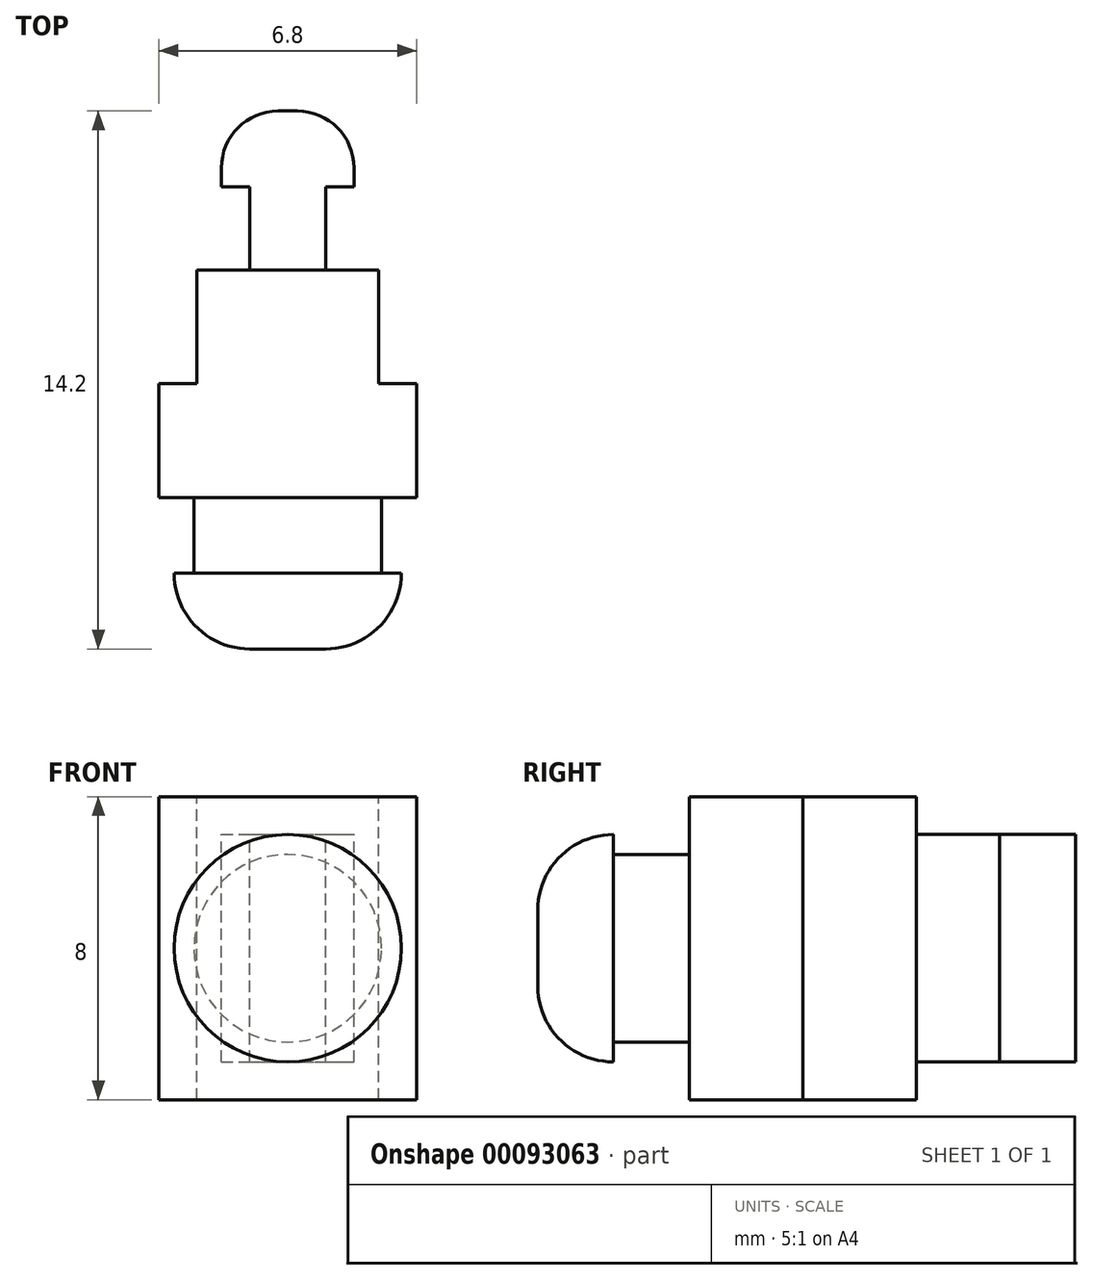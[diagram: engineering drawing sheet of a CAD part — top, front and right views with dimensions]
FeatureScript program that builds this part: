
annotation { "Feature Type Name" : "Feature", "Feature Type Description" : "" }
export const myFeature = defineFeature(function(context is Context, id is Id, definition is map)
    precondition{}
    {
        {
            var Q0;
            Q0=qCreatedBy(makeId("Front.planeOp"),FACE);
            var sketch = newSketch(context, id + "F0", { "sketchPlane" : qUnion([Q0])});
            skCircle(sketch, "E0", {"center": v(0, 0) * mm, "radius": 2.48 * mm});
            skSolve(sketch);
        }
        {
            var Q0;
            Q0=makeQuery(id+"F0.imprint","IMPRINT",FACE,{"disambiguationData":[TD([[makeQuery(id+"F0.imprint","IMPRINT",EDGE,{"derivedFrom":sQuery(id+"F0.wireOp",EDGE,"E0")}),1.0]])]});
            extrude(context, id + "F1", {"entities" : qUnion([Q0]), "depth" : 2 * mm});
        }
        {
            var Q0;
            Q0=makeQuery(id+"F1.opExtrude","CAP_FACE",FACE,{"disambiguationData":[OSD([sQuery(id+"F0.wireOp",EDGE,"E0")])],"isStart":false});
            var sketch = newSketch(context, id + "F2", { "sketchPlane" : qUnion([Q0])});
            skCircle(sketch, "E1", {"center": v(0, 0) * mm, "radius": 3 * mm});
            skSolve(sketch);
        }
        {
            var Q0;
            Q0 = qSketchRegion(id + "F2", true);
            extrude(context, id + "F3", {"entities" : qUnion([Q0]), "operationType" : NewBodyOperationType.ADD, "depth" : 2 * mm});
        }
        {
            var Q0;
            Q0=makeQuery(id+"F3.opExtrude","CAP_EDGE",EDGE,{"disambiguationData":[OSD([sQuery(id+"F2.wireOp",EDGE,"E1")])],"isStart":false});
            fillet(context, id + "F4", {"entities" : qUnion([Q0]), "radius" : 2 * mm, "tangentPropagation" : true, "allowEdgeOverflow" : false});
        }
        {
            var Q0;
            Q0=makeQuery(id+"F1.opExtrude","CAP_FACE",FACE,{"disambiguationData":[OSD([sQuery(id+"F0.wireOp",EDGE,"E0")])],"isStart":true});
            var sketch = newSketch(context, id + "F5", { "sketchPlane" : qUnion([Q0])});
            skLineSegment(sketch, "E2.bottom", {"start": v(3.4, 4) * mm, "end": v(-3.4, 4) * mm});
            skLineSegment(sketch, "E2.top", {"start": v(3.4, -4) * mm, "end": v(-3.4, -4) * mm});
            skLineSegment(sketch, "E2.left", {"start": v(3.4, 4) * mm, "end": v(3.4, -4) * mm});
            skLineSegment(sketch, "E2.right", {"start": v(-3.4, 4) * mm, "end": v(-3.4, -4) * mm});
            skPoint(sketch, "E2.middle", {"position": v(0, 0) * mm});
            skSolve(sketch);
        }
        {
            var Q0;
            Q0=makeQuery(id+"F5.imprint","IMPRINT",FACE,{"disambiguationData":[TD([[makeQuery(id+"F5.imprint","IMPRINT",EDGE,{"derivedFrom":sQuery(id+"F5.wireOp",EDGE,"E2.bottom")}),1.0]])]});
            var Q1;
            Q1=makeQuery(id+"F5.imprint","IMPRINT",FACE,{"disambiguationData":[TD([[makeQuery(id+"F5.imprint","IMPRINT",EDGE,{"derivedFrom":makeQuery(id+"F1.opExtrude","CAP_EDGE",EDGE,{"disambiguationData":[OSD([sQuery(id+"F0.wireOp",EDGE,"E0")])],"isStart":true})}),-1.0]])]});
            extrude(context, id + "F6", {"entities" : qUnion([Q0, Q1]), "operationType" : NewBodyOperationType.ADD, "depth" : 3 * mm});
        }
        {
            var Q0;
            Q0=makeQuery(id+"F6.opExtrude","CAP_FACE",FACE,{"disambiguationData":[OSD([sQuery(id+"F5.wireOp",EDGE,"E2.bottom"),sQuery(id+"F5.wireOp",EDGE,"E2.top"),sQuery(id+"F5.wireOp",EDGE,"E2.left"),sQuery(id+"F5.wireOp",EDGE,"E2.right")])],"isStart":false});
            var sketch = newSketch(context, id + "F7", { "sketchPlane" : qUnion([Q0])});
            skLineSegment(sketch, "E3.bottom", {"start": v(2.4, -4) * mm, "end": v(-2.4, -4) * mm});
            skLineSegment(sketch, "E3.top", {"start": v(2.4, 4) * mm, "end": v(-2.4, 4) * mm});
            skLineSegment(sketch, "E3.left", {"start": v(2.4, -4) * mm, "end": v(2.4, 4) * mm});
            skLineSegment(sketch, "E3.right", {"start": v(-2.4, -4) * mm, "end": v(-2.4, 4) * mm});
            skPoint(sketch, "E3.middle", {"position": v(0, 0) * mm});
            skSolve(sketch);
        }
        {
            var Q0;
            Q0=makeQuery(id+"F7.imprint","IMPRINT",FACE,{"disambiguationData":[TD([[makeQuery(id+"F7.imprint","IMPRINT",EDGE,{"derivedFrom":sQuery(id+"F7.wireOp",EDGE,"E3.bottom")}),-1.0]])]});
            extrude(context, id + "F8", {"entities" : qUnion([Q0]), "operationType" : NewBodyOperationType.ADD, "depth" : 3 * mm});
        }
        {
            var Q0;
            Q0=makeQuery(id+"F8.opExtrude","CAP_FACE",FACE,{"disambiguationData":[OSD([sQuery(id+"F7.wireOp",EDGE,"E3.bottom"),sQuery(id+"F7.wireOp",EDGE,"E3.top"),sQuery(id+"F7.wireOp",EDGE,"E3.left"),sQuery(id+"F7.wireOp",EDGE,"E3.right")])],"isStart":false});
            var sketch = newSketch(context, id + "F9", { "sketchPlane" : qUnion([Q0])});
            skLineSegment(sketch, "E4.bottom", {"start": v(1, -3) * mm, "end": v(-1, -3) * mm});
            skLineSegment(sketch, "E4.top", {"start": v(1, 3) * mm, "end": v(-1, 3) * mm});
            skLineSegment(sketch, "E4.left", {"start": v(1, -3) * mm, "end": v(1, 3) * mm});
            skLineSegment(sketch, "E4.right", {"start": v(-1, -3) * mm, "end": v(-1, 3) * mm});
            skPoint(sketch, "E4.middle", {"position": v(0, 0) * mm});
            skSolve(sketch);
        }
        {
            var Q0;
            Q0=makeQuery(id+"F9.imprint","IMPRINT",FACE,{"disambiguationData":[TD([[makeQuery(id+"F9.imprint","IMPRINT",EDGE,{"derivedFrom":sQuery(id+"F9.wireOp",EDGE,"E4.bottom")}),-1.0]])]});
            extrude(context, id + "F10", {"entities" : qUnion([Q0]), "operationType" : NewBodyOperationType.ADD, "depth" : 2.2 * mm});
        }
        {
            var Q0;
            Q0=makeQuery(id+"F10.opExtrude","CAP_FACE",FACE,{"disambiguationData":[OSD([sQuery(id+"F9.wireOp",EDGE,"E4.bottom"),sQuery(id+"F9.wireOp",EDGE,"E4.top"),sQuery(id+"F9.wireOp",EDGE,"E4.left"),sQuery(id+"F9.wireOp",EDGE,"E4.right")])],"isStart":false});
            var sketch = newSketch(context, id + "F11", { "sketchPlane" : qUnion([Q0])});
            skLineSegment(sketch, "E5.bottom", {"start": v(1.75, -3) * mm, "end": v(-1.75, -3) * mm});
            skLineSegment(sketch, "E5.top", {"start": v(1.75, 3) * mm, "end": v(-1.75, 3) * mm});
            skLineSegment(sketch, "E5.left", {"start": v(1.75, -3) * mm, "end": v(1.75, 3) * mm});
            skLineSegment(sketch, "E5.right", {"start": v(-1.75, -3) * mm, "end": v(-1.75, 3) * mm});
            skPoint(sketch, "E5.middle", {"position": v(0, 0) * mm});
            skSolve(sketch);
        }
        {
            var Q0;
            {var subQ2=sQuery(id+"F11.wireOp",EDGE,"E5.right");Q0=makeQuery(id+"F11.imprint","IMPRINT",FACE,{"disambiguationData":[TD([[makeQuery(id+"F11.imprint","IMPRINT",EDGE,{"derivedFrom":subQ2}),-1.0]])]});}
            var Q1;
            {var subQ1=makeQuery(id+"F10.opExtrude","CAP_EDGE",EDGE,{"disambiguationData":[OSD([sQuery(id+"F9.wireOp",EDGE,"E4.left")])],"isStart":false});Q1=makeQuery(id+"F11.imprint","IMPRINT",FACE,{"disambiguationData":[TD([[makeQuery(id+"F11.imprint","IMPRINT",EDGE,{"derivedFrom":subQ1}),1.0]])]});}
            var Q2;
            {var subQ2=sQuery(id+"F11.wireOp",EDGE,"E5.left");Q2=makeQuery(id+"F11.imprint","IMPRINT",FACE,{"disambiguationData":[TD([[makeQuery(id+"F11.imprint","IMPRINT",EDGE,{"derivedFrom":subQ2}),1.0]])]});}
            extrude(context, id + "F12", {"entities" : qUnion([Q0, Q1, Q2]), "operationType" : NewBodyOperationType.ADD, "depth" : 2 * mm});
        }
        {
            var Q0;
            Q0=makeQuery(id+"F12.opExtrude","CAP_EDGE",EDGE,{"disambiguationData":[OSD([sQuery(id+"F11.wireOp",EDGE,"E5.right")])],"isStart":false});
            var Q1;
            Q1=makeQuery(id+"F12.opExtrude","CAP_EDGE",EDGE,{"disambiguationData":[OSD([sQuery(id+"F11.wireOp",EDGE,"E5.left")])],"isStart":false});
            fillet(context, id + "F13", {"entities" : qUnion([Q0, Q1]), "radius" : 1.5 * mm, "tangentPropagation" : true, "allowEdgeOverflow" : false});
        }
    });
